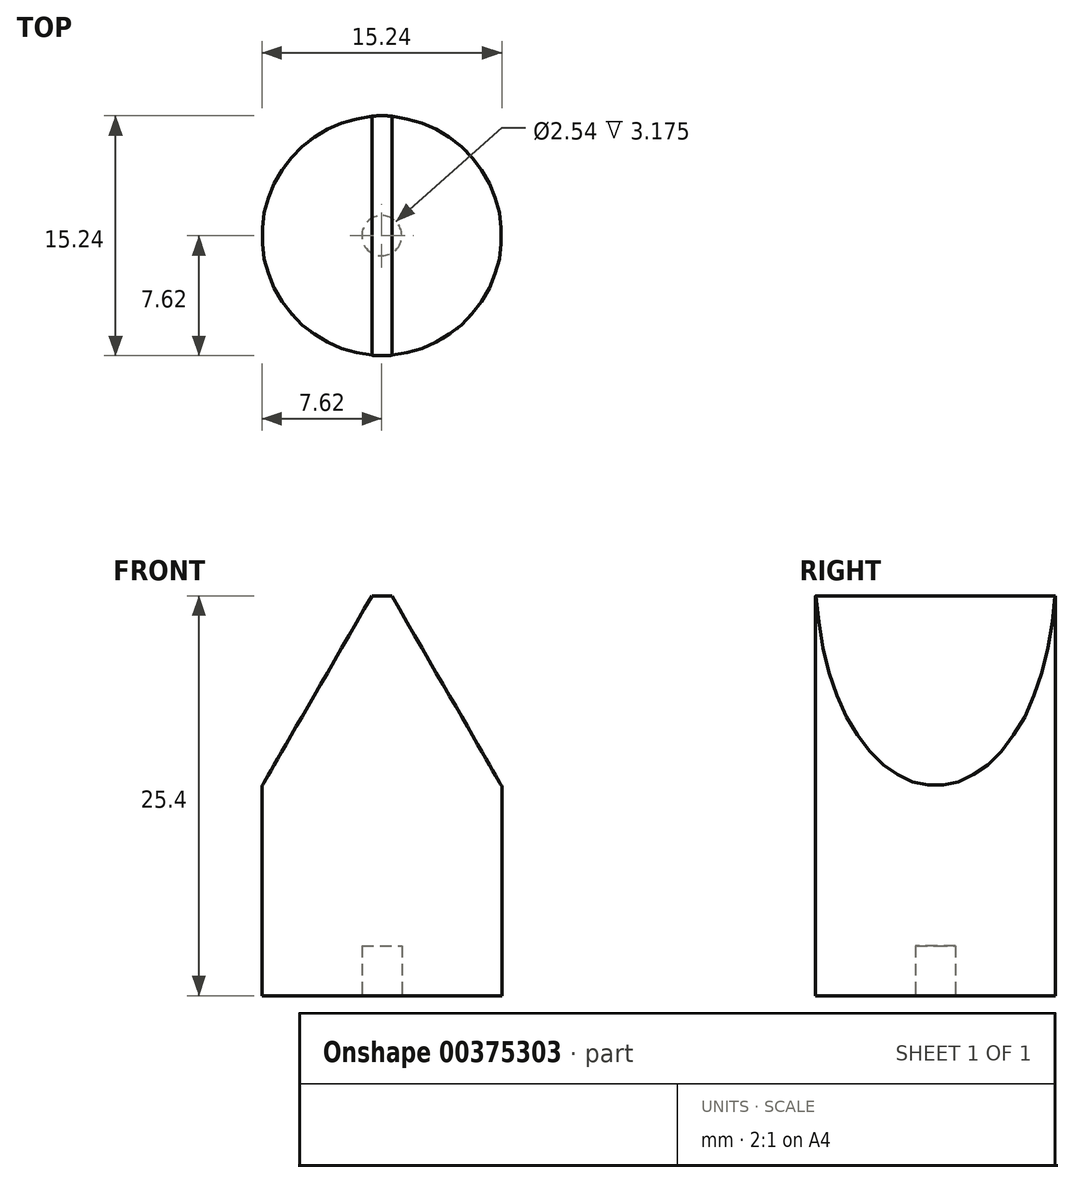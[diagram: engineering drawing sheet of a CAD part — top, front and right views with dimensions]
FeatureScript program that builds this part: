
annotation { "Feature Type Name" : "Feature", "Feature Type Description" : "" }
export const myFeature = defineFeature(function(context is Context, id is Id, definition is map)
    precondition{}
    {
        {
            var Q0;
            Q0=qCreatedBy(makeId("Top.planeOp"),FACE);
            var sketch = newSketch(context, id + "F0", { "sketchPlane" : qUnion([Q0])});
            skCircle(sketch, "E0", {"center": v(0, 0) * mm, "radius": 7.62 * mm});
            skSolve(sketch);
        }
        {
            var Q0;
            Q0 = qSketchRegion(id + "F0", true);
            extrude(context, id + "F1", {"entities" : qUnion([Q0]), "depth" : 25.4 * mm, "offsetDistance" : 25.4 * mm});
        }
        {
            var Q0;
            Q0=qCreatedBy(makeId("Front.planeOp"),FACE);
            var sketch = newSketch(context, id + "F2", { "sketchPlane" : qUnion([Q0])});
            skLineSegment(sketch, "E1", {"start": v(-7.62, 13.3) * mm, "end": v(0, 26.5) * mm});
            skLineSegment(sketch, "E2", {"start": v(0, 26.5) * mm, "end": v(7.62, 13.3) * mm});
            skLineSegment(sketch, "E3", {"start": v(-7.62, 13.3) * mm, "end": v(-7.62, 36.51) * mm});
            skLineSegment(sketch, "E4", {"start": v(-7.62, 36.51) * mm, "end": v(7.62, 36.51) * mm});
            skLineSegment(sketch, "E5", {"start": v(7.62, 36.51) * mm, "end": v(7.62, 13.3) * mm});
            skPoint(sketch, "E6", {"position": v(0, 36.51) * mm});
            skLineSegment(sketch, "E7", {"start": v(-0.64, 25.4) * mm, "end": v(0.64, 25.4) * mm});
            skSolve(sketch);
        }
        {
            var Q0;
            Q0 = qSketchRegion(id + "F2", true);
            extrude(context, id + "F3", {"entities" : qUnion([Q0]), "operationType" : NewBodyOperationType.REMOVE, "endBound" : BoundingType.THROUGH_ALL, "oppositeDirection" : true, "depth" : 25.4 * mm, "offsetDistance" : 25.4 * mm, "hasSecondDirection" : true, "secondDirectionBound" : SecondDirectionBoundingType.THROUGH_ALL, "secondDirectionOppositeDirection" : false, "secondDirectionDepth" : 25.4 * mm});
        }
        {
            var Q0;
            Q0=makeQuery(id+"F1.opExtrude","CAP_FACE",FACE,{"disambiguationData":[OSD([sQuery(id+"F0.wireOp",EDGE,"E0")])],"isStart":true});
            var sketch = newSketch(context, id + "F4", { "sketchPlane" : qUnion([Q0])});
            skCircle(sketch, "E8", {"center": v(0, 0) * mm, "radius": 1.27 * mm});
            skSolve(sketch);
        }
        {
            var Q0;
            Q0 = qSketchRegion(id + "F4", true);
            extrude(context, id + "F5", {"entities" : qUnion([Q0]), "operationType" : NewBodyOperationType.REMOVE, "oppositeDirection" : true, "depth" : 3.17 * mm, "offsetDistance" : 25.4 * mm});
        }
    });
